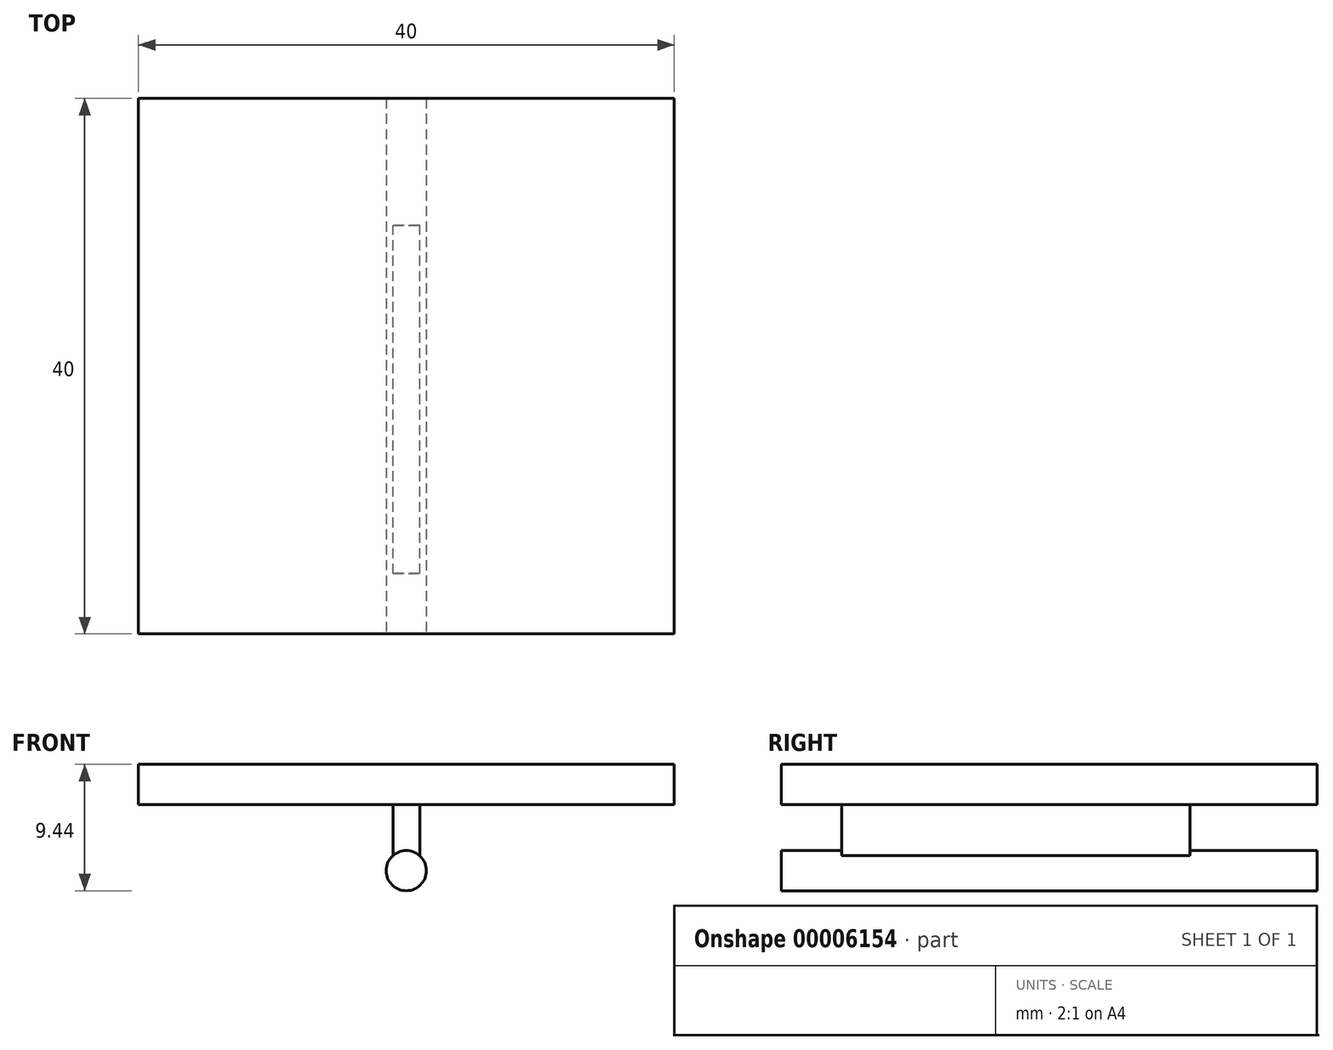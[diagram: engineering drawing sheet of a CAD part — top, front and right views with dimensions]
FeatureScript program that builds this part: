
annotation { "Feature Type Name" : "Feature", "Feature Type Description" : "" }
export const myFeature = defineFeature(function(context is Context, id is Id, definition is map)
    precondition{}
    {
        {
            var Q0;
            Q0=qCreatedBy(makeId("Top.planeOp"),FACE);
            var sketch = newSketch(context, id + "F0", { "sketchPlane" : qUnion([Q0])});
            skLineSegment(sketch, "E0.bottom", {"start": v(-87.58, -17.86) * mm, "end": v(-47.58, -17.86) * mm});
            skLineSegment(sketch, "E0.top", {"start": v(-87.58, 17.14) * mm, "end": v(-47.58, 17.14) * mm});
            skLineSegment(sketch, "E0.left", {"start": v(-87.58, -17.86) * mm, "end": v(-87.58, 17.14) * mm});
            skLineSegment(sketch, "E0.right", {"start": v(-47.58, -17.86) * mm, "end": v(-47.58, 17.14) * mm});
            skLineSegment(sketch, "E1.bottom", {"start": v(-68.58, -13.36) * mm, "end": v(-66.58, -13.36) * mm});
            skLineSegment(sketch, "E1.top", {"start": v(-68.58, 12.64) * mm, "end": v(-66.58, 12.64) * mm});
            skLineSegment(sketch, "E1.left", {"start": v(-68.58, -13.36) * mm, "end": v(-68.58, 12.64) * mm});
            skLineSegment(sketch, "E1.right", {"start": v(-66.58, -13.36) * mm, "end": v(-66.58, 12.64) * mm});
            skPoint(sketch, "E2", {"position": v(-87.58, -0.36) * mm});
            skPoint(sketch, "E3", {"position": v(-47.58, -0.36) * mm});
            skPoint(sketch, "E4", {"position": v(-67.58, 17.14) * mm});
            skPoint(sketch, "E5", {"position": v(-68.58, -0.36) * mm});
            skPoint(sketch, "E6", {"position": v(-67.58, 12.64) * mm});
            skSolve(sketch);
        }
        {
            var Q0;
            Q0 = qSketchRegion(id + "F0", true);
            var Q1;
            Q1=makeQuery(id+"F0.imprint","IMPRINT",FACE,{"disambiguationData":[TD([[makeQuery(id+"F0.imprint","IMPRINT",EDGE,{"derivedFrom":sQuery(id+"F0.wireOp",EDGE,"E1.bottom")}),1.0]])]});
            extrude(context, id + "F1", {"entities" : qUnion([Q0, Q1]), "depth" : 3 * mm});
        }
        {
            var Q0;
            Q0=makeQuery(id+"F0.imprint","IMPRINT",FACE,{"disambiguationData":[TD([[makeQuery(id+"F0.imprint","IMPRINT",EDGE,{"derivedFrom":sQuery(id+"F0.wireOp",EDGE,"E1.bottom")}),1.0]])]});
            extrude(context, id + "F2", {"entities" : qUnion([Q0]), "operationType" : NewBodyOperationType.ADD, "oppositeDirection" : true, "depth" : 4 * mm});
        }
        {
            var Q0;
            Q0=makeQuery(id+"F1.opExtrude","SWEPT_FACE",FACE,{"disambiguationData":[OSD([sQuery(id+"F0.wireOp",EDGE,"E0.bottom")])]});
            cPlane(context, id + "F3", {"entities" : qUnion([Q0]), "cplaneType" : CPlaneType.OFFSET, "offset" : 0 * mm, "width" : 150 * mm, "height" : 150 * mm});
        }
        {
            var Q0;
            Q0=qCreatedBy(id+"F3.planeOp",FACE);
            var sketch = newSketch(context, id + "F4", { "sketchPlane" : qUnion([Q0])});
            skCircle(sketch, "E7", {"center": v(-67.58, -4.94) * mm, "radius": 1.5 * mm});
            skPoint(sketch, "E8", {"position": v(-67.58, -4) * mm});
            skSolve(sketch);
        }
        {
            var Q0;
            Q0=makeQuery(id+"F1.opExtrude","SWEPT_FACE",FACE,{"disambiguationData":[OSD([sQuery(id+"F0.wireOp",EDGE,"E0.bottom")])]});
            var Q1;
            Q1=makeQuery(id+"F4.imprint","IMPRINT",FACE,{"disambiguationData":[TD([[makeQuery(id+"F4.imprint","IMPRINT",EDGE,{"derivedFrom":sQuery(id+"F4.wireOp",EDGE,"E7")}),1.0]])]});
            extrude(context, id + "F5", {"entities" : qUnion([Q0, Q1]), "operationType" : NewBodyOperationType.ADD, "oppositeDirection" : true, "depth" : 40 * mm});
        }
    });
